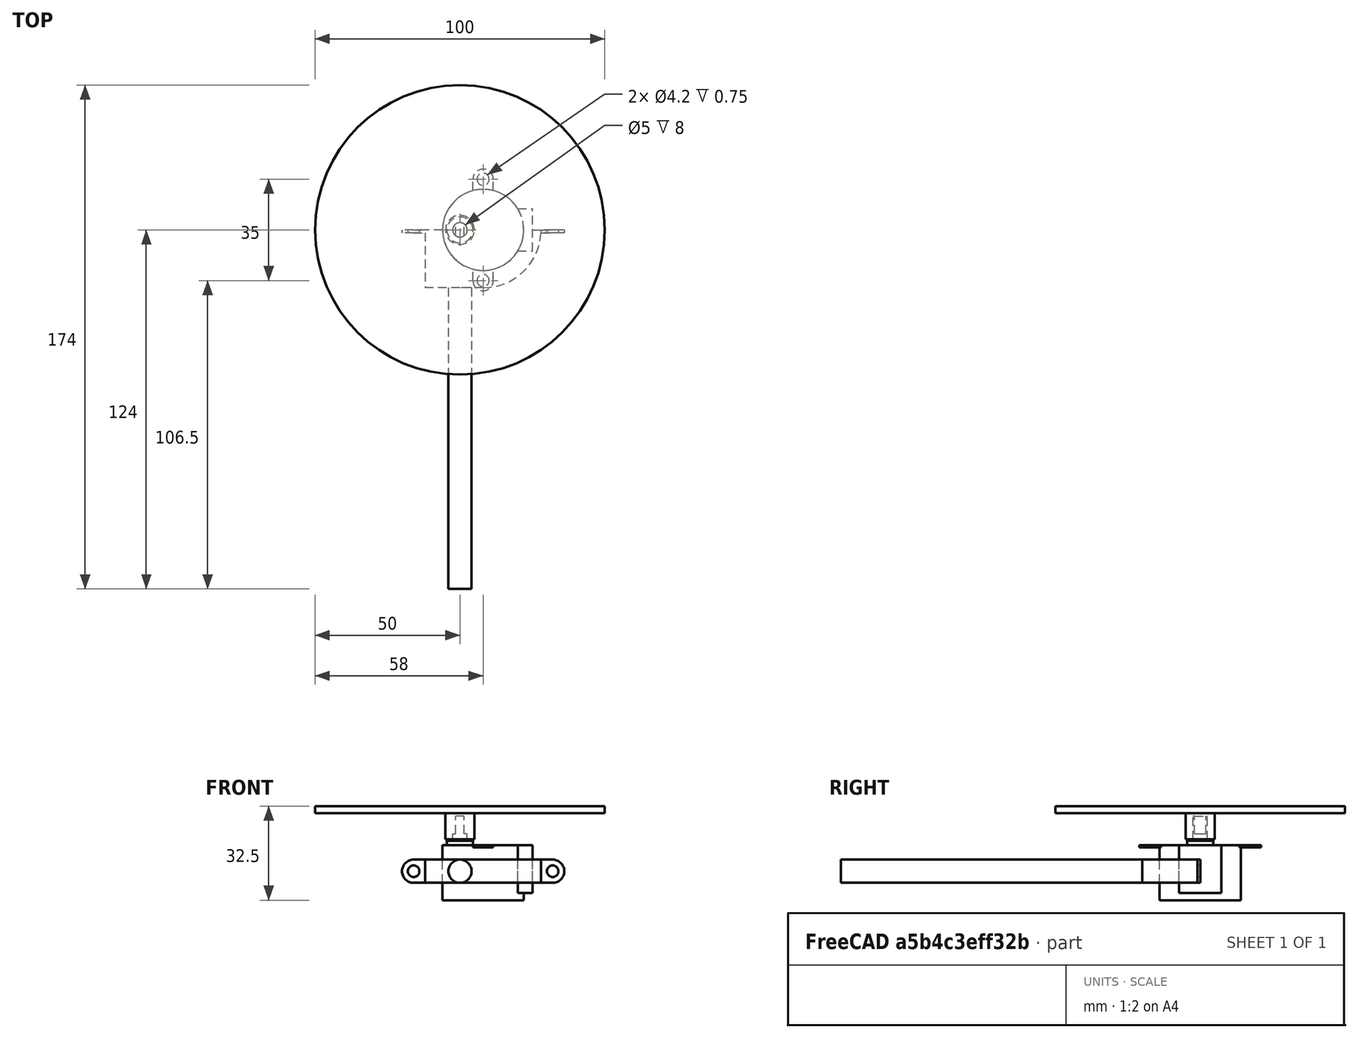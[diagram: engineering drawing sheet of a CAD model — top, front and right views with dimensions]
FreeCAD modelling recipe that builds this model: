
FCSTD DOCUMENT  (FreeCAD 0.16R6706 (Git))
Label: S2H-bottom-motor
License: All rights reserved
LicenseURL: http://en.wikipedia.org/wiki/All_rights_reserved
objects: Part::Cylinder×29, Part::Cut×16, Part::Box×15, Part::MultiFuse×8
note: 68 computed .brp shape members not serialized (recipe doc carries the construction recipe); baked Part::Feature solids carry a one-line shape summary decoded from their .brp

FEATURE [Part::Cylinder] Cylinder
  Angle = 360
  Height = 19
  Radius = 14
FEATURE [Part::Cylinder] Cylinder001
  Angle = 360
  Height = 1.5
  Placement = pos=(-8,0,19) rot=(0,0,1;0rad)
  Radius = 4.5
FEATURE [Part::Cylinder] Cylinder003
  Angle = 360
  Height = 8.5
  Placement = pos=(-8,0,20.5) rot=(0,0,1;0rad)
  Radius = 2.5
FEATURE [Part::Cylinder] Cylinder004
  Angle = 360
  Height = 2
  Placement = pos=(0,-17.5,18) rot=(0,0,1;0rad)
  Radius = 2.1
FEATURE [Part::Cylinder] Cylinder005
  Angle = 360
  Height = 2
  Placement = pos=(0,17.5,18) rot=(0,0,1;0rad)
  Radius = 2.1
FEATURE [Part::Cylinder] Cylinder006
  Angle = 360
  Height = 0.75
  Placement = pos=(0,-17.5,18) rot=(0,0,1;0rad)
  Radius = 3.5
FEATURE [Part::Cylinder] Cylinder007
  Angle = 360
  Height = 0.75
  Placement = pos=(0,17.5,18) rot=(0,0,1;0rad)
  Radius = 3.5
FEATURE [Part::Box] Box  label="Cube"
  Height = 0.75
  Length = 7
  Placement = pos=(-3.5,-17.5,18) rot=(0,0,1;0rad)
  Width = 35
FEATURE [Part::MultiFuse] Fusion
  Placement = pos=(0,0,0.25) rot=(0,0,1;0rad)
  Shapes = -> [Cylinder006,Cylinder007,Box]
FEATURE [Part::Cut] Cut
  Base = -> Fusion
  Tool = -> Cylinder004
FEATURE [Part::Cut] Cut001
  Base = -> Cut
  Tool = -> Cylinder005
FEATURE [Part::Box] Box001  label="Cube001"
  Height = 16.5
  Length = 17
  Placement = pos=(0,-7.3,2.5) rot=(0,0,1;0rad)
  Width = 14.6
FEATURE [Part::Box] Box002  label="Cube002"
  Height = 6
  Length = 1
  Placement = pos=(-6.5,-2.5,23) rot=(0,0,1;0rad)
  Width = 5
FEATURE [Part::Box] Box003  label="Cube003"
  Height = 6
  Length = 1
  Placement = pos=(-10.5,-2.5,23) rot=(0,0,1;0rad)
  Width = 5
FEATURE [Part::Cut] Cut002
  Base = -> Cylinder003
  Tool = -> Box002
FEATURE [Part::Cut] Cut003
  Base = -> Cut002
  Tool = -> Box003
FEATURE [Part::MultiFuse] Fusion001  label="motor"
  Placement = pos=(8,0,-10) rot=(0,0,1;0rad)
  Shapes = -> [Cut003,Box001,Cut001,Cylinder001,Cylinder]
FEATURE [Part::Cylinder] Cylinder008
  Angle = 360
  Height = 110
  Placement = pos=(-8,-14,10) rot=(1,0,0;1.5708rad)
  Radius = 4
FEATURE [Part::Cylinder] Cylinder009
  Angle = 90
  Height = 8
  Placement = pos=(0,0,6) rot=(0,0,-1;1.5708rad)
  Radius = 20
FEATURE [Part::Box] Box004  label="Cube004"
  Height = 8
  Length = 20
  Placement = pos=(0,0,6) rot=(0,0,1;3.14159rad)
  Width = 20
FEATURE [Part::Cylinder] Cylinder010
  Angle = 360
  Height = 1
  Placement = pos=(24,0,10) rot=(1,0,0;1.5708rad)
  Radius = 4
FEATURE [Part::Box] Box005  label="Cube005"
  Height = 8
  Length = 4
  Placement = pos=(20,-1,6) rot=(0,0,1;0rad)
  Width = 1
FEATURE [Part::Cylinder] Cylinder011
  Angle = 360
  Height = 1
  Placement = pos=(-24,0,10) rot=(1,0,0;1.5708rad)
  Radius = 4
FEATURE [Part::Box] Box006  label="Cube006"
  Height = 8
  Length = 4
  Placement = pos=(-24,-1,6) rot=(0,0,1;0rad)
  Width = 1
FEATURE [Part::MultiFuse] Fusion002
  Shapes = -> [Cylinder008,Cylinder009,Box004,Cylinder010,Box005,Cylinder011,Box006]
FEATURE [Part::Cylinder] Cylinder012
  Angle = 360
  Height = 19
  Radius = 14
FEATURE [Part::Cylinder] Cylinder013
  Angle = 360
  Height = 1.5
  Placement = pos=(-8,0,19) rot=(0,0,1;0rad)
  Radius = 4.5
FEATURE [Part::Cylinder] Cylinder014
  Angle = 360
  Height = 8.5
  Placement = pos=(-8,0,20.5) rot=(0,0,1;0rad)
  Radius = 2.5
FEATURE [Part::Cylinder] Cylinder015
  Angle = 360
  Height = 2
  Placement = pos=(0,-17.5,18) rot=(0,0,1;0rad)
  Radius = 2.1
FEATURE [Part::Cylinder] Cylinder016
  Angle = 360
  Height = 2
  Placement = pos=(0,17.5,18) rot=(0,0,1;0rad)
  Radius = 2.1
FEATURE [Part::Cylinder] Cylinder017
  Angle = 360
  Height = 0.75
  Placement = pos=(0,-17.5,18) rot=(0,0,1;0rad)
  Radius = 3.5
FEATURE [Part::Cylinder] Cylinder018
  Angle = 360
  Height = 0.75
  Placement = pos=(0,17.5,18) rot=(0,0,1;0rad)
  Radius = 3.5
FEATURE [Part::Box] Box007  label="Cube007"
  Height = 0.75
  Length = 7
  Placement = pos=(-3.5,-17.5,18) rot=(0,0,1;0rad)
  Width = 35
FEATURE [Part::MultiFuse] Fusion003
  Placement = pos=(0,0,0.25) rot=(0,0,1;0rad)
  Shapes = -> [Cylinder017,Cylinder018,Box007]
FEATURE [Part::Cut] Cut004
  Base = -> Fusion003
  Tool = -> Cylinder015
FEATURE [Part::Cut] Cut005
  Base = -> Cut004
  Tool = -> Cylinder016
FEATURE [Part::Box] Box008  label="Cube008"
  Height = 16.5
  Length = 17
  Placement = pos=(0,-7.3,2.5) rot=(0,0,1;0rad)
  Width = 14.6
FEATURE [Part::Box] Box009  label="Cube009"
  Height = 6
  Length = 1
  Placement = pos=(-6.5,-2.5,23) rot=(0,0,1;0rad)
  Width = 5
FEATURE [Part::Box] Box010  label="Cube010"
  Height = 6
  Length = 1
  Placement = pos=(-10.5,-2.5,23) rot=(0,0,1;0rad)
  Width = 5
FEATURE [Part::Cut] Cut006
  Base = -> Cylinder014
  Tool = -> Box009
FEATURE [Part::Cut] Cut007
  Base = -> Cut006
  Tool = -> Box010
FEATURE [Part::MultiFuse] Fusion004
  Shapes = -> [Cut007,Box008,Cut005,Cylinder013,Cylinder012]
FEATURE [Part::Cut] Cut008
  Base = -> Fusion002
  Placement = pos=(8,0,-10) rot=(0,0,1;0rad)
  Tool = -> Fusion004
FEATURE [Part::Cylinder] Cylinder019
  Angle = 360
  Height = 2.5
  Placement = pos=(0,0,20) rot=(0,0,1;0rad)
  Radius = 50
FEATURE [Part::Cylinder] Cylinder020
  Angle = 360
  Height = 9
  Placement = pos=(0,0,11) rot=(0,0,1;0rad)
  Radius = 5
FEATURE [Part::Cylinder] Cylinder021
  Angle = 360
  Height = 19
  Radius = 14
FEATURE [Part::Cylinder] Cylinder022
  Angle = 360
  Height = 1.5
  Placement = pos=(-8,0,19) rot=(0,0,1;0rad)
  Radius = 4.5
FEATURE [Part::Cylinder] Cylinder023
  Angle = 360
  Height = 8.5
  Placement = pos=(-8,0,20.5) rot=(0,0,1;0rad)
  Radius = 2.5
FEATURE [Part::Cylinder] Cylinder024
  Angle = 360
  Height = 2
  Placement = pos=(0,-17.5,18) rot=(0,0,1;0rad)
  Radius = 2.1
FEATURE [Part::Cylinder] Cylinder025
  Angle = 360
  Height = 2
  Placement = pos=(0,17.5,18) rot=(0,0,1;0rad)
  Radius = 2.1
FEATURE [Part::Cylinder] Cylinder026
  Angle = 360
  Height = 0.75
  Placement = pos=(0,-17.5,18) rot=(0,0,1;0rad)
  Radius = 3.5
FEATURE [Part::Cylinder] Cylinder027
  Angle = 360
  Height = 0.75
  Placement = pos=(0,17.5,18) rot=(0,0,1;0rad)
  Radius = 3.5
FEATURE [Part::Box] Box011  label="Cube011"
  Height = 0.75
  Length = 7
  Placement = pos=(-3.5,-17.5,18) rot=(0,0,1;0rad)
  Width = 35
FEATURE [Part::MultiFuse] Fusion005
  Placement = pos=(0,0,0.25) rot=(0,0,1;0rad)
  Shapes = -> [Cylinder026,Cylinder027,Box011]
FEATURE [Part::Cut] Cut009
  Base = -> Fusion005
  Tool = -> Cylinder024
FEATURE [Part::Cut] Cut010
  Base = -> Cut009
  Tool = -> Cylinder025
FEATURE [Part::Box] Box012  label="Cube012"
  Height = 16.5
  Length = 17
  Placement = pos=(0,-7.3,2.5) rot=(0,0,1;0rad)
  Width = 14.6
FEATURE [Part::Box] Box013  label="Cube013"
  Height = 6
  Length = 1
  Placement = pos=(-6.5,-2.5,23) rot=(0,0,1;0rad)
  Width = 5
FEATURE [Part::Box] Box014  label="Cube014"
  Height = 6
  Length = 1
  Placement = pos=(-10.5,-2.5,23) rot=(0,0,1;0rad)
  Width = 5
FEATURE [Part::Cut] Cut011
  Base = -> Cylinder023
  Tool = -> Box013
FEATURE [Part::Cut] Cut012
  Base = -> Cut011
  Tool = -> Box014
FEATURE [Part::MultiFuse] Fusion006
  Placement = pos=(8,0,-10) rot=(0,0,1;0rad)
  Shapes = -> [Cut012,Box012,Cut010,Cylinder022,Cylinder021]
FEATURE [Part::Cut] Cut013
  Base = -> Cylinder020
  Tool = -> Fusion006
FEATURE [Part::MultiFuse] Fusion007  label="bottom plate"
  Shapes = -> [Cylinder019,Cut013]
FEATURE [Part::Cylinder] Cylinder028
  Angle = 360
  Height = 10
  Placement = pos=(-16,5,0) rot=(1,0,0;1.5708rad)
  Radius = 2
FEATURE [Part::Cylinder] Cylinder029
  Angle = 360
  Height = 10
  Placement = pos=(32,5,0) rot=(1,0,0;1.5708rad)
  Radius = 2
FEATURE [Part::Cut] Cut014
  Base = -> Cut008
  Tool = -> Cylinder028
FEATURE [Part::Cut] Cut015  label="holder"
  Base = -> Cut014
  Tool = -> Cylinder029
